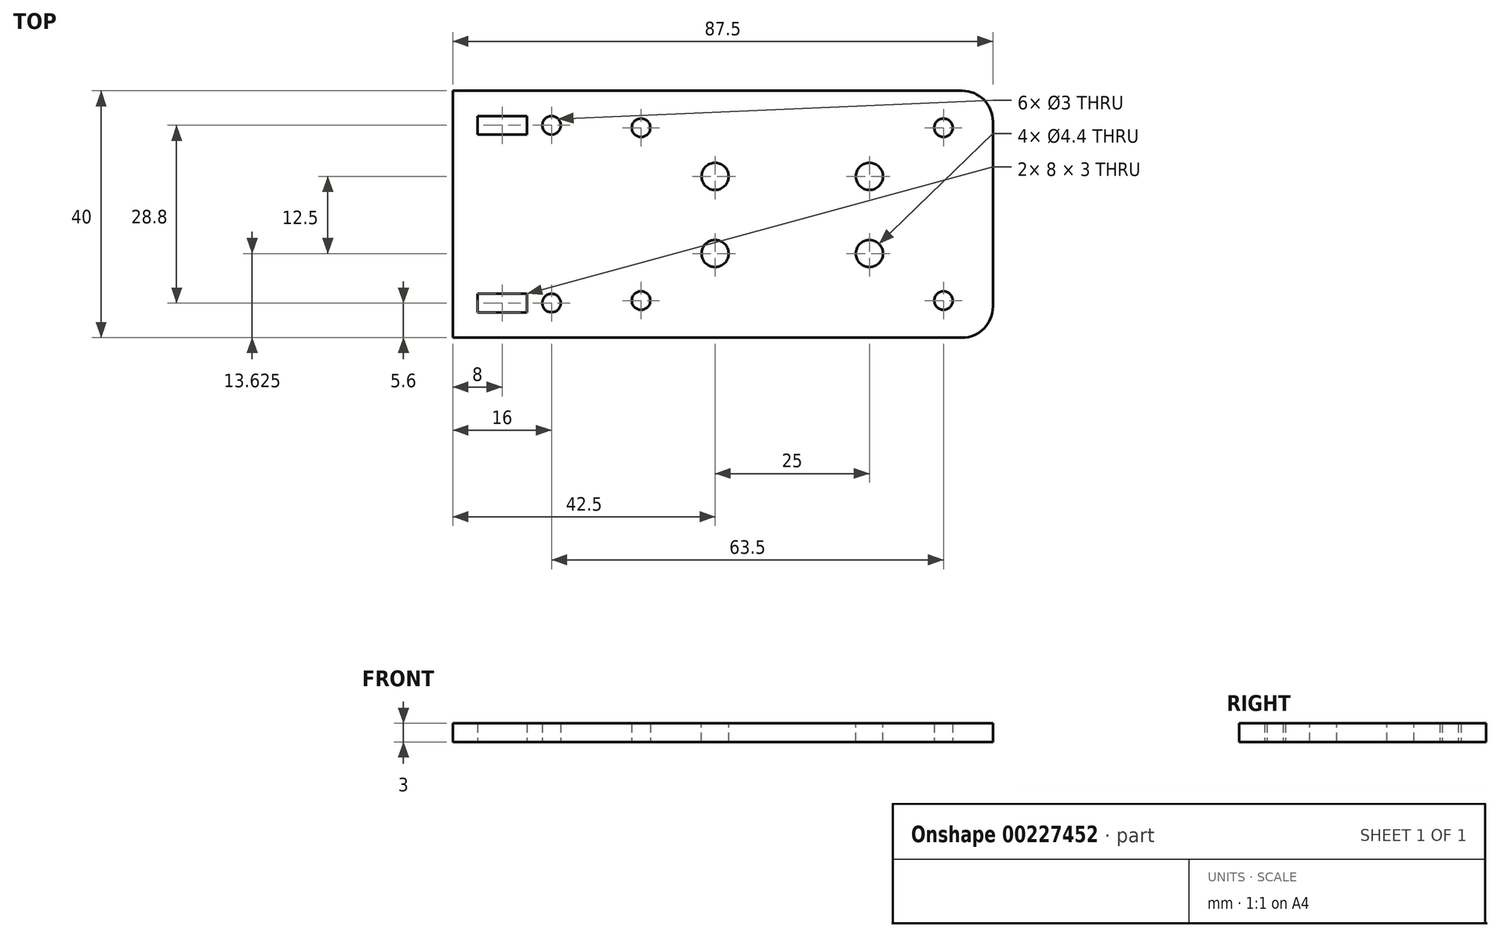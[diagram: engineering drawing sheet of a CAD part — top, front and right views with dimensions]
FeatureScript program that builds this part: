
annotation { "Feature Type Name" : "Feature", "Feature Type Description" : "" }
export const myFeature = defineFeature(function(context is Context, id is Id, definition is map)
    precondition{}
    {
        {
            assignVariable(context, id + "F0", {"name" : "Thickness", "anyValue" : 3});
        }
        {
            var Q0;
            Q0=qCreatedBy(makeId("Top.planeOp"),FACE);
            var sketch = newSketch(context, id + "F1", { "sketchPlane" : qUnion([Q0])});
            skLineSegment(sketch, "E0.bottom", {"start": v(32.5, -20) * mm, "end": v(-55, -20) * mm});
            skLineSegment(sketch, "E0.top", {"start": v(32.5, 20) * mm, "end": v(-55, 20) * mm});
            skLineSegment(sketch, "E0.left", {"start": v(32.5, -20) * mm, "end": v(32.5, 20) * mm});
            skLineSegment(sketch, "E0.right", {"start": v(-55, -20) * mm, "end": v(-55, 20) * mm});
            skLineSegment(sketch, "E1", {"start": v(-55, -14) * mm, "end": v(32.5, -14) * mm, "construction": true});
            skPoint(sketch, "E2", {"position": v(-47, -14.4) * mm});
            skLineSegment(sketch, "E3.bottom", {"start": v(-43, -15.9) * mm, "end": v(-51, -15.9) * mm});
            skLineSegment(sketch, "E3.top", {"start": v(-43, -12.9) * mm, "end": v(-51, -12.9) * mm});
            skLineSegment(sketch, "E3.left", {"start": v(-43, -15.9) * mm, "end": v(-43, -12.9) * mm});
            skLineSegment(sketch, "E3.right", {"start": v(-51, -15.9) * mm, "end": v(-51, -12.9) * mm});
            skPoint(sketch, "E4.MirrorP", {"position": v(-47, 14.4) * mm});
            skLineSegment(sketch, "E5.MirrorCS", {"start": v(-43, 12.9) * mm, "end": v(-51, 12.9) * mm});
            skLineSegment(sketch, "E6.MirrorCS", {"start": v(-43, 15.9) * mm, "end": v(-43, 12.9) * mm});
            skLineSegment(sketch, "E7.MirrorCS", {"start": v(-51, 15.9) * mm, "end": v(-51, 12.9) * mm});
            skLineSegment(sketch, "E8.MirrorCS", {"start": v(-43, 15.9) * mm, "end": v(-51, 15.9) * mm});
            skCircle(sketch, "E9", {"center": v(-24.5, -14) * mm, "radius": 1.5 * mm});
            skCircle(sketch, "E10.MirrorC", {"center": v(24.5, -14) * mm, "radius": 1.5 * mm});
            skCircle(sketch, "E11.MirrorC", {"center": v(-24.5, 14) * mm, "radius": 1.5 * mm});
            skCircle(sketch, "E12.MirrorC", {"center": v(24.5, 14) * mm, "radius": 1.5 * mm});
            skPoint(sketch, "E13", {"position": v(-39, -14.4) * mm});
            skCircle(sketch, "E14", {"center": v(-39, -14.4) * mm, "radius": 1.5 * mm});
            skCircle(sketch, "E15.MirrorC", {"center": v(-39, 14.4) * mm, "radius": 1.5 * mm});
            skSolve(sketch);
        }
        {
            var Q0;
            Q0=makeQuery(id+"F1.imprint","IMPRINT",FACE,{"disambiguationData":[TD([[makeQuery(id+"F1.imprint","IMPRINT",EDGE,{"derivedFrom":sQuery(id+"F1.wireOp",EDGE,"E0.bottom")}),-1.0]])]});
            extrude(context, id + "F2", {"entities" : qUnion([Q0]), "depth" : (getVariable(context, 'Thickness')) * mm});
        }
        {
            var Q0;
            Q0=makeQuery(id+"F2.opExtrude","CAP_FACE",FACE,{"disambiguationData":[OSD([sQuery(id+"F1.wireOp",EDGE,"E0.bottom"),sQuery(id+"F1.wireOp",EDGE,"E0.top"),sQuery(id+"F1.wireOp",EDGE,"E0.left"),sQuery(id+"F1.wireOp",EDGE,"E0.right"),sQuery(id+"F1.wireOp",EDGE,"E3.bottom"),sQuery(id+"F1.wireOp",EDGE,"E3.top"),sQuery(id+"F1.wireOp",EDGE,"E3.left"),sQuery(id+"F1.wireOp",EDGE,"E3.right"),sQuery(id+"F1.wireOp",EDGE,"4e853eb8-a7be-464d-ba3a-89b9014984401.MirrorCS"),sQuery(id+"F1.wireOp",EDGE,"4e853eb8-a7be-464d-ba3a-89b9014984402.MirrorCS"),sQuery(id+"F1.wireOp",EDGE,"4e853eb8-a7be-464d-ba3a-89b9014984403.MirrorCS"),sQuery(id+"F1.wireOp",EDGE,"4e853eb8-a7be-464d-ba3a-89b9014984404.MirrorCS"),sQuery(id+"F1.wireOp",EDGE,"E5.MirrorCS"),sQuery(id+"F1.wireOp",EDGE,"E6.MirrorCS"),sQuery(id+"F1.wireOp",EDGE,"E7.MirrorCS"),sQuery(id+"F1.wireOp",EDGE,"520273c5-be23-472e-a46e-9842cf4ddfa16.MirrorCS"),sQuery(id+"F1.wireOp",EDGE,"E8.MirrorCS"),sQuery(id+"F1.wireOp",EDGE,"520273c5-be23-472e-a46e-9842cf4ddfa18.MirrorCS"),sQuery(id+"F1.wireOp",EDGE,"520273c5-be23-472e-a46e-9842cf4ddfa19.MirrorCS"),sQuery(id+"F1.wireOp",EDGE,"E40.MirrorCS"),sQuery(id+"F1.wireOp",EDGE,"E9"),sQuery(id+"F1.wireOp",EDGE,"E10.MirrorC"),sQuery(id+"F1.wireOp",EDGE,"E11.MirrorC"),sQuery(id+"F1.wireOp",EDGE,"E12.MirrorC")])],"isStart":false});
            var sketch = newSketch(context, id + "F3", { "sketchPlane" : qUnion([Q0])});
            skPoint(sketch, "E16", {"position": v(-12.5, 6.12) * mm});
            skPoint(sketch, "E17.0.1.0", {"position": v(-12.5, -6.38) * mm});
            skPoint(sketch, "E17.1.0.0", {"position": v(12.5, 6.12) * mm});
            skPoint(sketch, "E17.1.1.0", {"position": v(12.5, -6.38) * mm});
            skLineSegment(sketch, "E17.direction1", {"start": v(-12.5, 6.12) * mm, "end": v(12.5, 6.12) * mm, "construction": true});
            skLineSegment(sketch, "E17.direction2", {"start": v(-12.5, 6.12) * mm, "end": v(-12.5, -6.37) * mm, "construction": true});
            skSolve(sketch);
        }
        {
            var Q0;
            Q0=sQuery(id+"F3.wireOp",VERTEX,"E16");
            var Q1;
            Q1=sQuery(id+"F3.wireOp",VERTEX,"E17.0.1.0");
            var Q2;
            Q2=sQuery(id+"F3.wireOp",VERTEX,"E17.1.0.0");
            var Q3;
            Q3=sQuery(id+"F3.wireOp",VERTEX,"E17.1.1.0");
            var Q4;
            Q4=makeQuery(id+"F2.opExtrude","SWEPT_BODY",BODY,{"disambiguationData":[OSD([sQuery(id+"F1.wireOp",EDGE,"E0.bottom"),sQuery(id+"F1.wireOp",EDGE,"E0.top"),sQuery(id+"F1.wireOp",EDGE,"E0.left"),sQuery(id+"F1.wireOp",EDGE,"E0.right"),sQuery(id+"F1.wireOp",EDGE,"E3.bottom"),sQuery(id+"F1.wireOp",EDGE,"E3.top"),sQuery(id+"F1.wireOp",EDGE,"E3.left"),sQuery(id+"F1.wireOp",EDGE,"E3.right"),sQuery(id+"F1.wireOp",EDGE,"4e853eb8-a7be-464d-ba3a-89b9014984401.MirrorCS"),sQuery(id+"F1.wireOp",EDGE,"4e853eb8-a7be-464d-ba3a-89b9014984402.MirrorCS"),sQuery(id+"F1.wireOp",EDGE,"4e853eb8-a7be-464d-ba3a-89b9014984403.MirrorCS"),sQuery(id+"F1.wireOp",EDGE,"4e853eb8-a7be-464d-ba3a-89b9014984404.MirrorCS"),sQuery(id+"F1.wireOp",EDGE,"E5.MirrorCS"),sQuery(id+"F1.wireOp",EDGE,"E6.MirrorCS"),sQuery(id+"F1.wireOp",EDGE,"E7.MirrorCS"),sQuery(id+"F1.wireOp",EDGE,"520273c5-be23-472e-a46e-9842cf4ddfa16.MirrorCS"),sQuery(id+"F1.wireOp",EDGE,"E8.MirrorCS"),sQuery(id+"F1.wireOp",EDGE,"520273c5-be23-472e-a46e-9842cf4ddfa18.MirrorCS"),sQuery(id+"F1.wireOp",EDGE,"520273c5-be23-472e-a46e-9842cf4ddfa19.MirrorCS"),sQuery(id+"F1.wireOp",EDGE,"E40.MirrorCS"),sQuery(id+"F1.wireOp",EDGE,"E9"),sQuery(id+"F1.wireOp",EDGE,"E10.MirrorC"),sQuery(id+"F1.wireOp",EDGE,"E11.MirrorC"),sQuery(id+"F1.wireOp",EDGE,"E12.MirrorC")])]});
            hole(context, id + "F4", {"style" : HoleStyle.SIMPLE, "endStyle" : HoleEndStyle.THROUGH, "standardTappedOrClearance" : lookupTablePath({ "standard" : "ISO", "fit" : "Normal", "size" : "M4", "type" : "Clearance" }), "standardBlindInLast" : lookupTablePath({ "fit" : "Standard", "standard" : "ISO", "size" : "M4", "type" : "Clearance" }), "holeDiameter" : 4.4 * mm, "tappedDepth" : 12 * mm, "tapClearance" : 3, "locations" : qUnion([Q0, Q1, Q2, Q3]), "scope" : qUnion([Q4])});
        }
        {
            var Q0;
            Q0=makeQuery(id+"F2.opExtrude","SWEPT_EDGE",EDGE,{"disambiguationData":[OSD([sQuery(id+"F1.wireOp",EDGE,"E0.top"),sQuery(id+"F1.wireOp",EDGE,"E0.left")])]});
            var Q1;
            Q1=makeQuery(id+"F2.opExtrude","SWEPT_EDGE",EDGE,{"disambiguationData":[OSD([sQuery(id+"F1.wireOp",EDGE,"E0.bottom"),sQuery(id+"F1.wireOp",EDGE,"E0.left")])]});
            fillet(context, id + "F5", {"entities" : qUnion([Q0, Q1]), "radius" : 5 * mm, "tangentPropagation" : true, "allowEdgeOverflow" : false});
        }
    });
